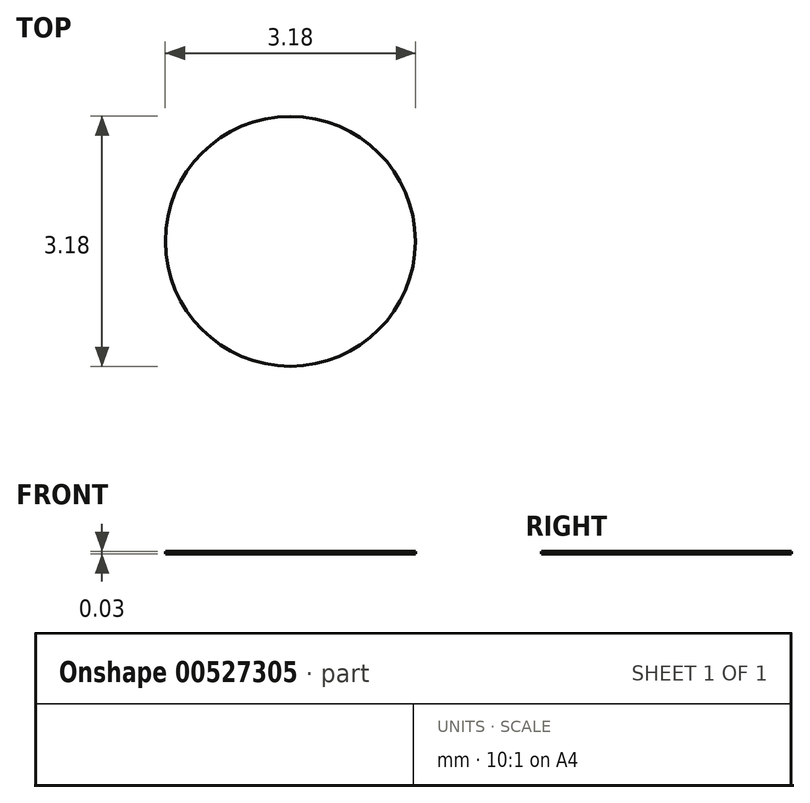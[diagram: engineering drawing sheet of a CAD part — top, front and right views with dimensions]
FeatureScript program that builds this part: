
annotation { "Feature Type Name" : "Feature", "Feature Type Description" : "" }
export const myFeature = defineFeature(function(context is Context, id is Id, definition is map)
    precondition{}
    {
        {
            var Q0;
            Q0=qCreatedBy(makeId("Top.planeOp"),FACE);
            var sketch = newSketch(context, id + "F0", { "sketchPlane" : qUnion([Q0])});
            skCircle(sketch, "E0", {"center": v(0, 0) * mm, "radius": 1.59 * mm});
            skSolve(sketch);
        }
        {
            var Q0;
            Q0=makeQuery(id+"F0.imprint","IMPRINT",FACE,{"disambiguationData":[TD([[makeQuery(id+"F0.imprint","IMPRINT",EDGE,{"derivedFrom":sQuery(id+"F0.wireOp",EDGE,"E0")}),1.0]])]});
            extrude(context, id + "F1", {"entities" : qUnion([Q0]), "depth" : 3 / 101.6 * mm, "offsetDistance" : 25 * mm});
        }
    });
